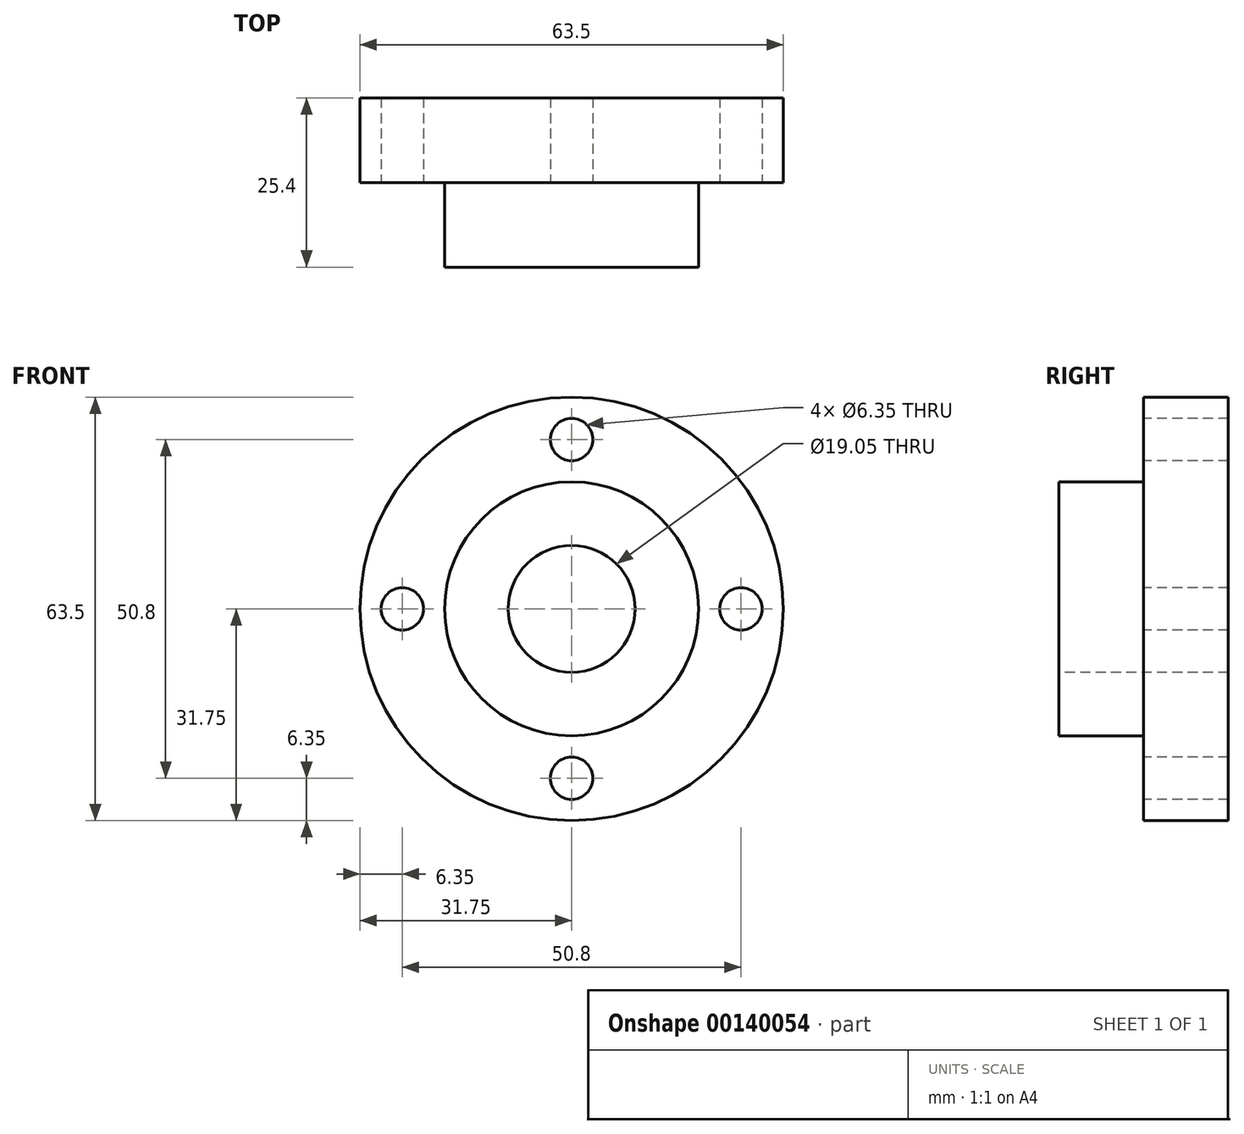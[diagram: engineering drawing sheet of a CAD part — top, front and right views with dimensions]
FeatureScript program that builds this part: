
annotation { "Feature Type Name" : "Feature", "Feature Type Description" : "" }
export const myFeature = defineFeature(function(context is Context, id is Id, definition is map)
    precondition{}
    {
        {
            var Q0;
            Q0=qCreatedBy(makeId("Front.planeOp"),FACE);
            var sketch = newSketch(context, id + "F0", { "sketchPlane" : qUnion([Q0])});
            skCircle(sketch, "E0", {"center": v(0, 0) * mm, "radius": 31.75 * mm});
            skLineSegment(sketch, "E1", {"start": v(0, 0) * mm, "end": v(31.75, 0) * mm, "construction": true});
            skLineSegment(sketch, "E2", {"start": v(0, 0) * mm, "end": v(-19.05, 0) * mm, "construction": true});
            skSolve(sketch);
        }
        {
            var Q0;
            Q0 = qSketchRegion(id + "F0", true);
            extrude(context, id + "F1", {"entities" : qUnion([Q0]), "depth" : 12.7 * mm});
        }
        {
            var Q0;
            Q0=makeQuery(id+"F1.opExtrude","CAP_FACE",FACE,{"disambiguationData":[OSD([sQuery(id+"F0.wireOp",EDGE,"E0")])],"isStart":false});
            var sketch = newSketch(context, id + "F2", { "sketchPlane" : qUnion([Q0])});
            skLineSegment(sketch, "E3", {"start": v(0, 0) * mm, "end": v(-19.05, 0) * mm, "construction": true});
            skCircle(sketch, "E4", {"center": v(0, 0) * mm, "radius": 19.05 * mm});
            skSolve(sketch);
        }
        {
            var Q0;
            Q0 = qSketchRegion(id + "F2", true);
            extrude(context, id + "F3", {"entities" : qUnion([Q0]), "operationType" : NewBodyOperationType.ADD, "depth" : 12.7 * mm});
        }
        {
            var Q0;
            Q0=makeQuery(id+"F3.opExtrude","CAP_FACE",FACE,{"disambiguationData":[OSD([sQuery(id+"F2.wireOp",EDGE,"E4")])],"isStart":false});
            var sketch = newSketch(context, id + "F4", { "sketchPlane" : qUnion([Q0])});
            skCircle(sketch, "E5", {"center": v(0, 0) * mm, "radius": 9.53 * mm});
            skSolve(sketch);
        }
        {
            var Q0;
            Q0 = qSketchRegion(id + "F4", true);
            extrude(context, id + "F5", {"entities" : qUnion([Q0]), "operationType" : NewBodyOperationType.REMOVE, "oppositeDirection" : true, "depth" : 25.4 * mm});
        }
        {
            var Q0;
            Q0=makeQuery(id+"F1.opExtrude","CAP_FACE",FACE,{"disambiguationData":[OSD([sQuery(id+"F0.wireOp",EDGE,"E0")])],"isStart":false});
            var sketch = newSketch(context, id + "F6", { "sketchPlane" : qUnion([Q0])});
            skLineSegment(sketch, "E6", {"start": v(0, 0) * mm, "end": v(0, 36.1) * mm, "construction": true});
            skLineSegment(sketch, "E7", {"start": v(0, 0) * mm, "end": v(35.2, 0) * mm, "construction": true});
            skLineSegment(sketch, "E8", {"start": v(0, 0) * mm, "end": v(0, -35.01) * mm, "construction": true});
            skLineSegment(sketch, "E9", {"start": v(0, 0) * mm, "end": v(-38.36, 0) * mm, "construction": true});
            skCircle(sketch, "E10", {"center": v(25.4, 0) * mm, "radius": 3.18 * mm});
            skCircle(sketch, "E11", {"center": v(0, 25.4) * mm, "radius": 3.18 * mm});
            skCircle(sketch, "E12", {"center": v(-25.4, 0) * mm, "radius": 3.18 * mm});
            skCircle(sketch, "E13", {"center": v(0, -25.4) * mm, "radius": 3.18 * mm});
            skSolve(sketch);
        }
        {
            var Q0;
            Q0 = qSketchRegion(id + "F6", true);
            extrude(context, id + "F7", {"entities" : qUnion([Q0]), "operationType" : NewBodyOperationType.REMOVE, "oppositeDirection" : true, "depth" : 12.7 * mm});
        }
    });
